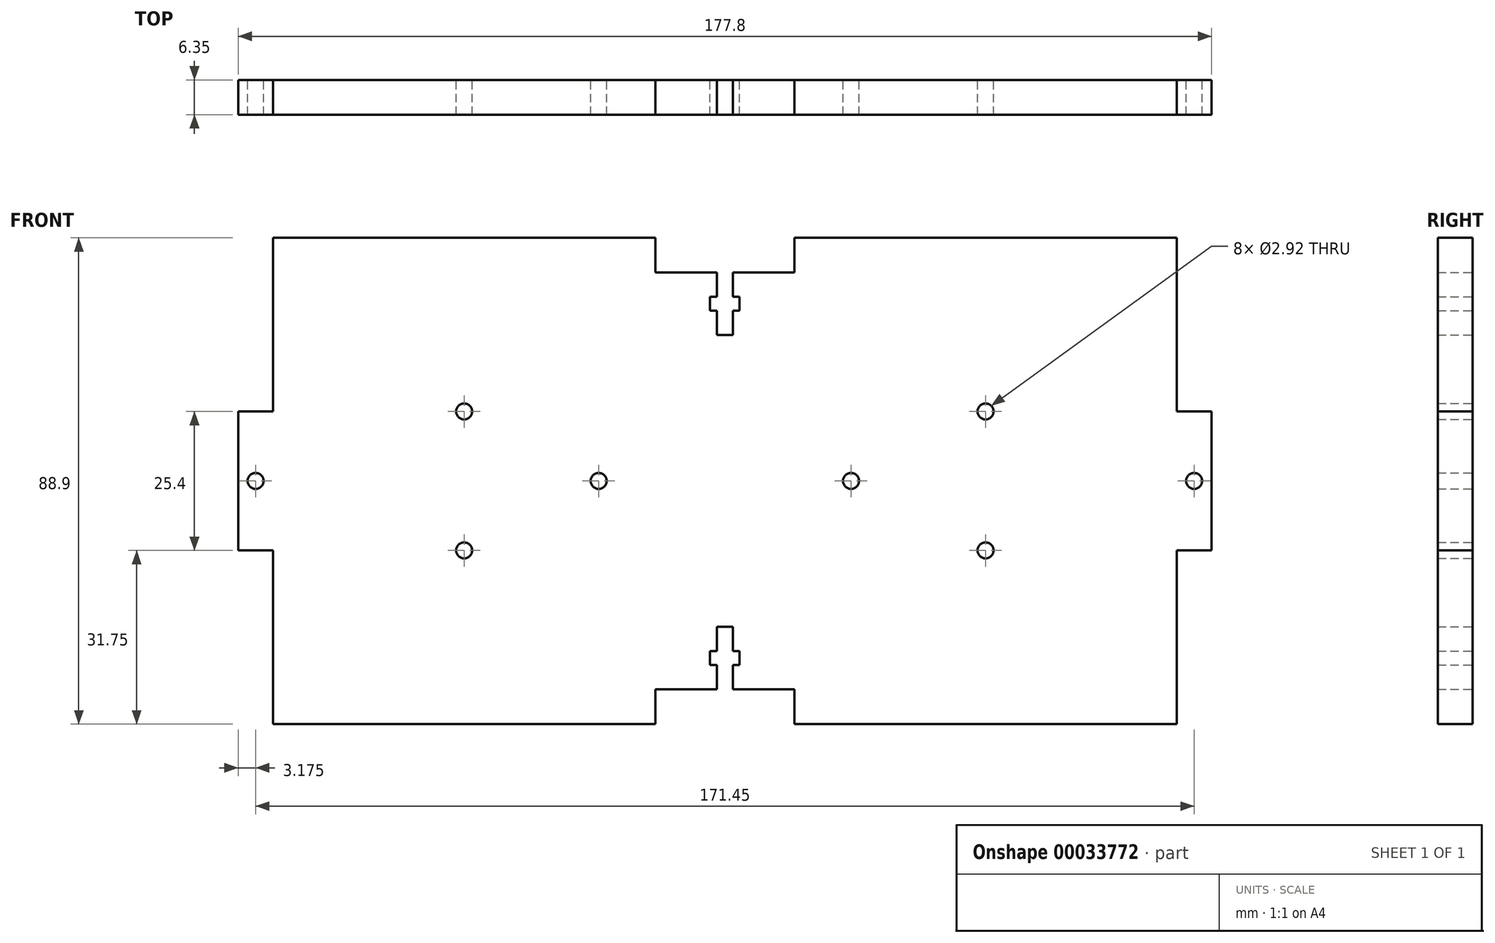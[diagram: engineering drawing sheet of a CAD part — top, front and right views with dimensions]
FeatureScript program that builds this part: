
annotation { "Feature Type Name" : "Feature", "Feature Type Description" : "" }
export const myFeature = defineFeature(function(context is Context, id is Id, definition is map)
    precondition{}
    {
        {
            var Q0;
            Q0=qCreatedBy(makeId("Front.planeOp"),FACE);
            var sketch = newSketch(context, id + "F0", { "sketchPlane" : qUnion([Q0])});
            skLineSegment(sketch, "E0.rect.top", {"start": v(82.55, 44.45) * mm, "end": v(12.7, 44.45) * mm});
            skLineSegment(sketch, "E0.rect.left", {"start": v(88.9, -12.7) * mm, "end": v(88.9, 12.7) * mm});
            skLineSegment(sketch, "E0.rect.right", {"start": v(-88.9, -12.7) * mm, "end": v(-88.9, 12.7) * mm});
            skPoint(sketch, "E0.rect.middle", {"position": v(0, 0) * mm});
            skLineSegment(sketch, "E1", {"start": v(0, 44.45) * mm, "end": v(0, -44.45) * mm, "construction": true});
            skLineSegment(sketch, "E2.0", {"start": v(82.55, 38.1) * mm, "end": v(-82.55, 38.1) * mm, "construction": true});
            skLineSegment(sketch, "E2.1", {"start": v(82.55, -38.1) * mm, "end": v(82.55, 38.1) * mm, "construction": true});
            skLineSegment(sketch, "E2.2", {"start": v(82.55, -38.1) * mm, "end": v(-82.55, -38.1) * mm, "construction": true});
            skLineSegment(sketch, "E2.3", {"start": v(-82.55, -38.1) * mm, "end": v(-82.55, 0) * mm, "construction": true});
            skLineSegment(sketch, "E3.0", {"start": v(-88.9, -12.7) * mm, "end": v(88.9, -12.7) * mm, "construction": true});
            skLineSegment(sketch, "E4.MirrorCS", {"start": v(-88.9, 12.7) * mm, "end": v(88.9, 12.7) * mm, "construction": true});
            skLineSegment(sketch, "E5.MirrorCS", {"start": v(12.7, 44.45) * mm, "end": v(12.7, -44.45) * mm, "construction": true});
            skLineSegment(sketch, "E6", {"start": v(-12.7, 44.45) * mm, "end": v(-12.7, 38.1) * mm, "construction": true});
            skLineSegment(sketch, "E7", {"start": v(-12.7, 38.1) * mm, "end": v(12.7, 38.1) * mm, "construction": true});
            skLineSegment(sketch, "E8", {"start": v(12.7, 38.1) * mm, "end": v(12.7, 44.45) * mm, "construction": true});
            skLineSegment(sketch, "E9.MirrorCS", {"start": v(-12.7, -44.45) * mm, "end": v(-12.7, -38.1) * mm});
            skLineSegment(sketch, "E10.MirrorCS", {"start": v(-12.7, -38.1) * mm, "end": v(-1.46, -38.1) * mm});
            skLineSegment(sketch, "E11.MirrorCS", {"start": v(12.7, -38.1) * mm, "end": v(12.7, -44.45) * mm});
            skLineSegment(sketch, "E12.trimOffspring", {"start": v(-12.7, 44.45) * mm, "end": v(-82.55, 44.45) * mm});
            skLineSegment(sketch, "E13", {"start": v(-12.7, 44.45) * mm, "end": v(-12.7, 38.1) * mm});
            skLineSegment(sketch, "E14", {"start": v(-12.7, 38.1) * mm, "end": v(-1.46, 38.1) * mm});
            skLineSegment(sketch, "E15", {"start": v(12.7, 38.1) * mm, "end": v(12.7, 44.45) * mm});
            skLineSegment(sketch, "E16", {"start": v(-88.9, 12.7) * mm, "end": v(-82.55, 12.7) * mm});
            skLineSegment(sketch, "E17", {"start": v(-82.55, 12.7) * mm, "end": v(-82.55, 44.45) * mm});
            skLineSegment(sketch, "E18.MirrorCS", {"start": v(-88.9, -12.7) * mm, "end": v(-82.55, -12.7) * mm});
            skLineSegment(sketch, "E19.MirrorCS", {"start": v(-82.55, -12.7) * mm, "end": v(-82.55, -44.45) * mm});
            skLineSegment(sketch, "E20.MirrorCS", {"start": v(82.55, 12.7) * mm, "end": v(82.55, 44.45) * mm});
            skLineSegment(sketch, "E21.MirrorCS", {"start": v(88.9, 12.7) * mm, "end": v(82.55, 12.7) * mm});
            skLineSegment(sketch, "E22.MirrorCS", {"start": v(88.9, -12.7) * mm, "end": v(82.55, -12.7) * mm, "construction": true});
            skLineSegment(sketch, "E23.MirrorCS", {"start": v(82.55, -12.7) * mm, "end": v(82.55, -44.45) * mm});
            skLineSegment(sketch, "E24", {"start": v(-88.9, 0) * mm, "end": v(-82.55, 0) * mm, "construction": true});
            skLineSegment(sketch, "E25", {"start": v(82.55, -12.7) * mm, "end": v(88.9, -12.7) * mm});
            skPoint(sketch, "E26.orphan", {"position": v(88.9, 44.45) * mm});
            skPoint(sketch, "E27.orphan", {"position": v(88.9, -44.45) * mm});
            skPoint(sketch, "E28.orphan", {"position": v(-88.9, -44.45) * mm});
            skPoint(sketch, "E29.orphan", {"position": v(-88.9, 44.45) * mm});
            skLineSegment(sketch, "E30", {"start": v(-82.55, 0) * mm, "end": v(-82.55, 38.1) * mm, "construction": true});
            skCircle(sketch, "E31", {"center": v(-85.73, 0) * mm, "radius": 1.46 * mm});
            skCircle(sketch, "E32.MirrorC", {"center": v(85.73, 0) * mm, "radius": 1.46 * mm});
            skLineSegment(sketch, "E33.0", {"start": v(-1.46, 44.45) * mm, "end": v(-1.46, -44.45) * mm, "construction": true});
            skLineSegment(sketch, "E34.MirrorCS", {"start": v(1.46, 44.45) * mm, "end": v(1.46, -44.45) * mm, "construction": true});
            skLineSegment(sketch, "E35", {"start": v(-12.7, 26.67) * mm, "end": v(12.7, 26.67) * mm, "construction": true});
            skLineSegment(sketch, "E36", {"start": v(-12.7, 26.67) * mm, "end": v(-12.7, -44.45) * mm, "construction": true});
            skLineSegment(sketch, "E37", {"start": v(-12.7, 38.1) * mm, "end": v(-12.7, 26.67) * mm, "construction": true});
            skLineSegment(sketch, "E38", {"start": v(-12.7, 32.39) * mm, "end": v(12.7, 32.39) * mm, "construction": true});
            skLineSegment(sketch, "E39.0", {"start": v(-12.7, 31.12) * mm, "end": v(12.7, 31.12) * mm, "construction": true});
            skLineSegment(sketch, "E40.MirrorCS", {"start": v(-12.7, 33.66) * mm, "end": v(12.7, 33.66) * mm, "construction": true});
            skLineSegment(sketch, "E41.0", {"start": v(-2.7, 44.45) * mm, "end": v(-2.7, -44.45) * mm, "construction": true});
            skLineSegment(sketch, "E42.MirrorCS", {"start": v(2.7, 44.45) * mm, "end": v(2.7, -44.45) * mm, "construction": true});
            skLineSegment(sketch, "E43", {"start": v(-1.46, 38.1) * mm, "end": v(-1.46, 33.66) * mm});
            skLineSegment(sketch, "E44", {"start": v(-1.46, 33.66) * mm, "end": v(-2.7, 33.66) * mm});
            skLineSegment(sketch, "E45", {"start": v(-2.7, 33.66) * mm, "end": v(-2.7, 31.12) * mm});
            skLineSegment(sketch, "E46", {"start": v(-2.7, 31.12) * mm, "end": v(-1.46, 31.12) * mm});
            skLineSegment(sketch, "E47", {"start": v(-1.46, 31.12) * mm, "end": v(-1.46, 26.67) * mm});
            skLineSegment(sketch, "E48", {"start": v(-1.46, 26.67) * mm, "end": v(1.46, 26.67) * mm});
            skLineSegment(sketch, "E49", {"start": v(1.46, 26.67) * mm, "end": v(1.46, 31.12) * mm});
            skLineSegment(sketch, "E50", {"start": v(1.46, 31.12) * mm, "end": v(2.7, 31.12) * mm});
            skLineSegment(sketch, "E51", {"start": v(2.7, 31.12) * mm, "end": v(2.7, 33.66) * mm});
            skLineSegment(sketch, "E52", {"start": v(2.7, 33.66) * mm, "end": v(1.46, 33.66) * mm});
            skLineSegment(sketch, "E53", {"start": v(1.46, 33.66) * mm, "end": v(1.46, 38.1) * mm});
            skLineSegment(sketch, "E54.trimOffspring", {"start": v(1.46, 38.1) * mm, "end": v(12.7, 38.1) * mm});
            skLineSegment(sketch, "E55.MirrorCS", {"start": v(-1.46, -38.1) * mm, "end": v(-1.46, -33.66) * mm});
            skLineSegment(sketch, "E56.MirrorCS", {"start": v(-1.46, -33.66) * mm, "end": v(-2.7, -33.66) * mm});
            skLineSegment(sketch, "E57.MirrorCS", {"start": v(-2.7, -33.66) * mm, "end": v(-2.7, -31.12) * mm});
            skLineSegment(sketch, "E58.MirrorCS", {"start": v(-2.7, -31.12) * mm, "end": v(-1.46, -31.12) * mm});
            skLineSegment(sketch, "E59.MirrorCS", {"start": v(-1.46, -31.12) * mm, "end": v(-1.46, -26.67) * mm});
            skLineSegment(sketch, "E60.MirrorCS", {"start": v(-1.46, -26.67) * mm, "end": v(1.46, -26.67) * mm});
            skLineSegment(sketch, "E61.MirrorCS", {"start": v(1.46, -26.67) * mm, "end": v(1.46, -31.12) * mm});
            skLineSegment(sketch, "E62.MirrorCS", {"start": v(1.46, -31.12) * mm, "end": v(2.7, -31.12) * mm});
            skLineSegment(sketch, "E63.MirrorCS", {"start": v(2.7, -31.12) * mm, "end": v(2.7, -33.66) * mm});
            skLineSegment(sketch, "E64.MirrorCS", {"start": v(2.7, -33.66) * mm, "end": v(1.46, -33.66) * mm});
            skLineSegment(sketch, "E65.MirrorCS", {"start": v(1.46, -33.66) * mm, "end": v(1.46, -38.1) * mm});
            skLineSegment(sketch, "E66.trimOffspring", {"start": v(1.46, -38.1) * mm, "end": v(12.7, -38.1) * mm});
            skPoint(sketch, "E67.MirrorCS.end.orphan", {"position": v(82.55, -44.45) * mm});
            skPoint(sketch, "E68.MirrorCS.end.orphan", {"position": v(12.7, -44.45) * mm});
            skPoint(sketch, "E69.MirrorCS.end.orphan", {"position": v(-12.7, -44.45) * mm});
            skLineSegment(sketch, "E70", {"start": v(-82.55, -44.45) * mm, "end": v(-12.7, -44.45) * mm});
            skLineSegment(sketch, "E71", {"start": v(82.55, -44.45) * mm, "end": v(12.7, -44.45) * mm});
            skLineSegment(sketch, "E72", {"start": v(-47.63, 44.45) * mm, "end": v(-47.63, -44.45) * mm, "construction": true});
            skLineSegment(sketch, "E73", {"start": v(47.63, 44.45) * mm, "end": v(47.63, -44.45) * mm, "construction": true});
            skCircle(sketch, "E74", {"center": v(-47.63, 12.7) * mm, "radius": 1.46 * mm});
            skCircle(sketch, "E75.MirrorC", {"center": v(-47.63, -12.7) * mm, "radius": 1.46 * mm});
            skCircle(sketch, "E76.MirrorC", {"center": v(47.63, 12.7) * mm, "radius": 1.46 * mm});
            skCircle(sketch, "E77.MirrorC", {"center": v(47.63, -12.7) * mm, "radius": 1.46 * mm});
            skLineSegment(sketch, "E78.0", {"start": v(-27.94, 44.45) * mm, "end": v(-27.94, -44.45) * mm, "construction": true});
            skLineSegment(sketch, "E79.MirrorCS", {"start": v(27.94, 44.45) * mm, "end": v(27.94, -44.45) * mm, "construction": true});
            skLineSegment(sketch, "E80.MirrorCS", {"start": v(20.32, 44.45) * mm, "end": v(20.32, -44.45) * mm, "construction": true});
            skLineSegment(sketch, "E81", {"start": v(-20.32, 0) * mm, "end": v(88.9, 0) * mm, "construction": true});
            skLineSegment(sketch, "E82.0", {"start": v(-21.59, 44.45) * mm, "end": v(-21.59, -44.45) * mm, "construction": true});
            skLineSegment(sketch, "E83.0", {"start": v(-24.51, 44.45) * mm, "end": v(-24.51, -44.45) * mm, "construction": true});
            skLineSegment(sketch, "E84", {"start": v(-24.51, 0) * mm, "end": v(-21.59, 0) * mm, "construction": true});
            skCircle(sketch, "E85", {"center": v(-23.05, 0) * mm, "radius": 1.46 * mm});
            skCircle(sketch, "E86.MirrorC", {"center": v(23.05, 0) * mm, "radius": 1.46 * mm});
            skSolve(sketch);
        }
        {
            var Q0;
            Q0=makeQuery(id+"F0.imprint","IMPRINT",FACE,{"disambiguationData":[TD([[makeQuery(id+"F0.imprint","IMPRINT",EDGE,{"derivedFrom":sQuery(id+"F0.wireOp",EDGE,"E0.rect.top")}),1.0]])]});
            extrude(context, id + "F1", {"entities" : qUnion([Q0]), "depth" : 6.35 * mm});
        }
    });
